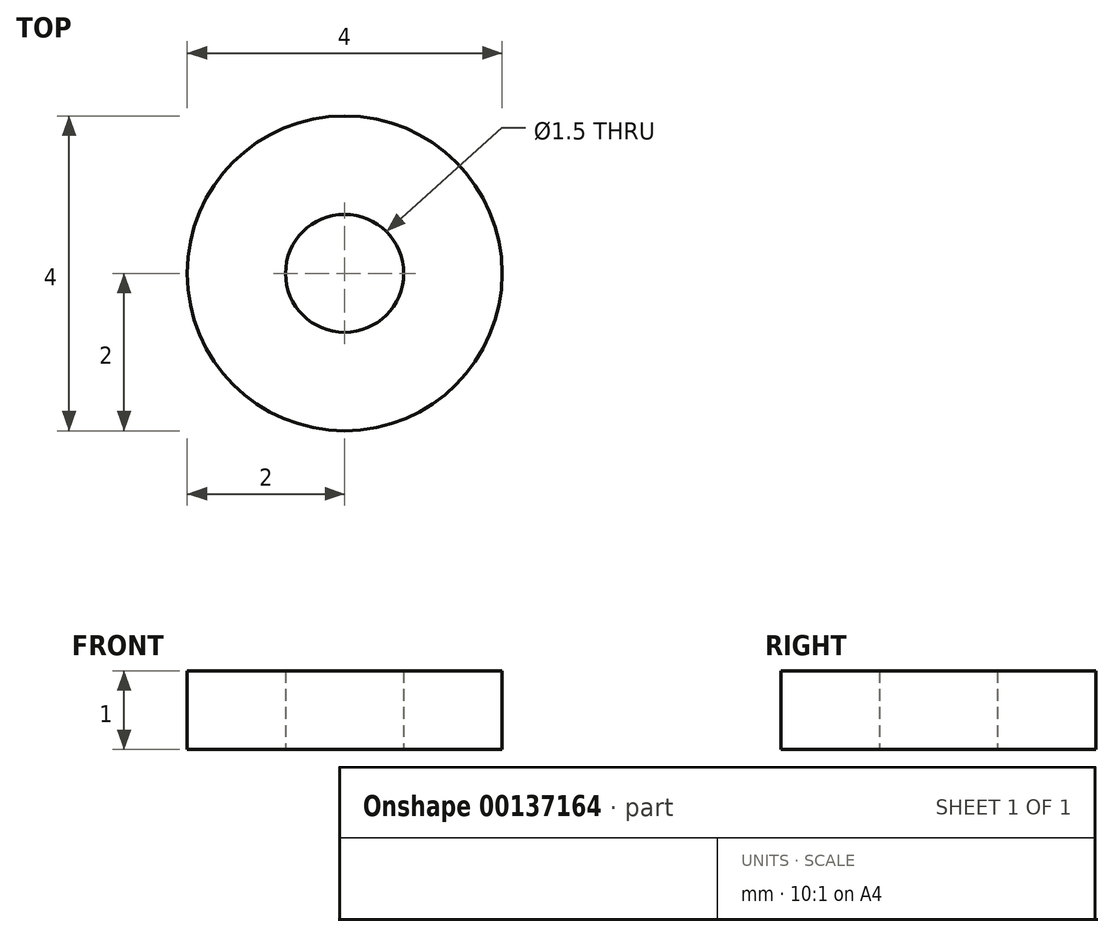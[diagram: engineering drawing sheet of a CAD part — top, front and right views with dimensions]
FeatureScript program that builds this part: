
annotation { "Feature Type Name" : "Feature", "Feature Type Description" : "" }
export const myFeature = defineFeature(function(context is Context, id is Id, definition is map)
    precondition{}
    {
        {
            var Q0;
            Q0=qCreatedBy(makeId("Top.planeOp"),FACE);
            var sketch = newSketch(context, id + "F0", { "sketchPlane" : qUnion([Q0])});
            skCircle(sketch, "E0", {"center": v(0, 0) * mm, "radius": 0.75 * mm});
            skCircle(sketch, "E1", {"center": v(0, 0) * mm, "radius": 2 * mm});
            skSolve(sketch);
        }
        {
            var Q0;
            Q0 = qSketchRegion(id + "F0", true);
            extrude(context, id + "F1", {"entities" : qUnion([Q0]), "depth" : 1 * mm});
        }
    });
